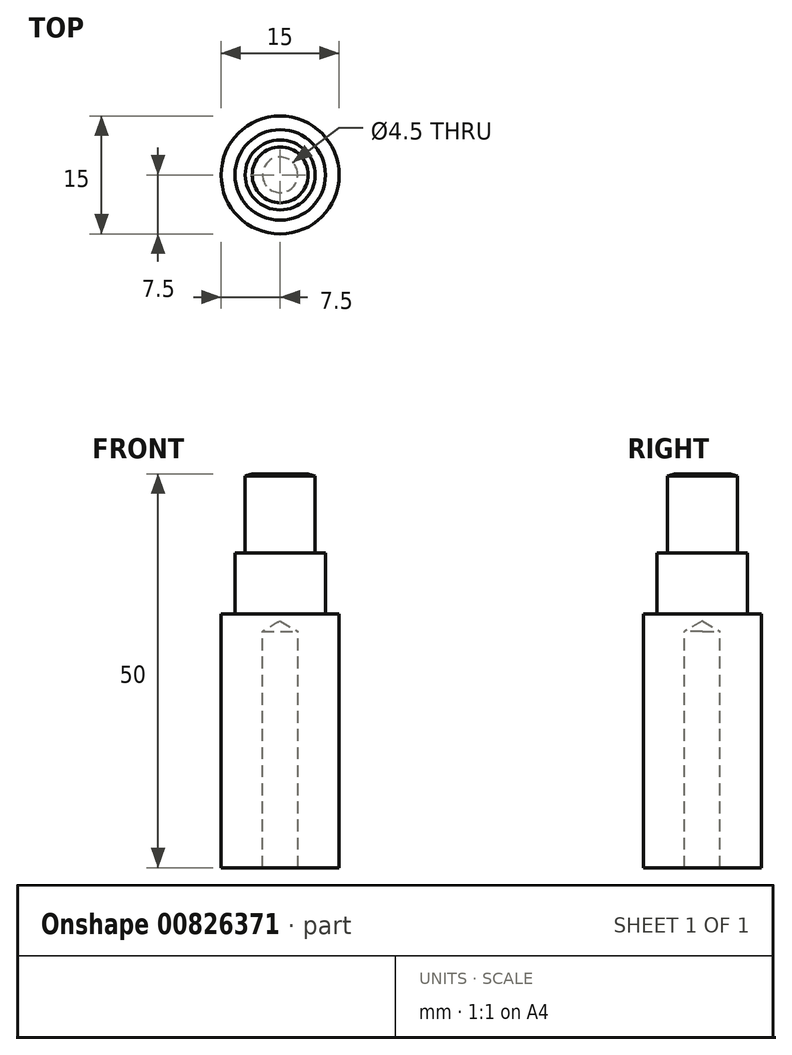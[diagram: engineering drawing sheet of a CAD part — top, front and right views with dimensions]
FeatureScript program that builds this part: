
annotation { "Feature Type Name" : "Feature", "Feature Type Description" : "" }
export const myFeature = defineFeature(function(context is Context, id is Id, definition is map)
    precondition{}
    {
        {
            var Q0;
            Q0=qCreatedBy(makeId("Front.planeOp"),FACE);
            var sketch = newSketch(context, id + "F0", { "sketchPlane" : qUnion([Q0])});
            skLineSegment(sketch, "E0", {"start": v(0, 0) * mm, "end": v(0, 50) * mm});
            skLineSegment(sketch, "E1", {"start": v(0, 50) * mm, "end": v(4.45, 50) * mm});
            skLineSegment(sketch, "E2", {"start": v(4.45, 50) * mm, "end": v(4.45, 40) * mm});
            skLineSegment(sketch, "E3", {"start": v(4.45, 40) * mm, "end": v(5.75, 40) * mm});
            skLineSegment(sketch, "E4", {"start": v(5.75, 40) * mm, "end": v(5.75, 32.2) * mm});
            skLineSegment(sketch, "E5", {"start": v(5.75, 32.2) * mm, "end": v(7.5, 32.2) * mm});
            skLineSegment(sketch, "E6", {"start": v(7.5, 32.2) * mm, "end": v(7.5, 0) * mm});
            skLineSegment(sketch, "E7", {"start": v(7.5, 0) * mm, "end": v(0, 0) * mm});
            skSolve(sketch);
        }
        {
            var Q0;
            Q0 = qSketchRegion(id + "F0", true);
            var Q1;
            Q1=sQuery(id+"F0.wireOp",EDGE,"E0");
            revolve(context, id + "F1", {"surfaceOperationType" : NewSurfaceOperationType.NEW, "entities" : qUnion([Q0]), "axis" : qUnion([Q1]), "revolveType" : RevolveType.FULL});
        }
        {
            var Q0;
            Q0=makeQuery(id+"F1.opRevolve","SWEPT_EDGE",EDGE,{"disambiguationData":[OSD([sQuery(id+"F0.wireOp",EDGE,"E1"),sQuery(id+"F0.wireOp",EDGE,"E2")])]});
            chamfer(context, id + "F2", {"entities" : qUnion([Q0]), "chamferType" : ChamferType.OFFSET_ANGLE, "width" : 8 * mm, "oppositeDirection" : false, "angle" : 15 * degree, "tangentPropagation" : true});
        }
        {
            var Q0;
            Q0=makeQuery(id+"F1.opRevolve","SWEPT_FACE",FACE,{"disambiguationData":[OSD([sQuery(id+"F0.wireOp",EDGE,"E7")])]});
            var sketch = newSketch(context, id + "F3", { "sketchPlane" : qUnion([Q0])});
            skPoint(sketch, "E8", {"position": v(0, 0) * mm});
            skSolve(sketch);
        }
        {
            var Q0;
            Q0=sQuery(id+"F3.wireOp",VERTEX,"E8");
            var Q1;
            Q1=makeQuery(id+"F1.opRevolve","SWEPT_BODY",BODY,{"disambiguationData":[OSD([sQuery(id+"F0.wireOp",EDGE,"E0"),sQuery(id+"F0.wireOp",EDGE,"E1"),sQuery(id+"F0.wireOp",EDGE,"E2"),sQuery(id+"F0.wireOp",EDGE,"E3"),sQuery(id+"F0.wireOp",EDGE,"E4"),sQuery(id+"F0.wireOp",EDGE,"E5"),sQuery(id+"F0.wireOp",EDGE,"E6"),sQuery(id+"F0.wireOp",EDGE,"E7")])]});
            hole(context, id + "F4", {"style" : HoleStyle.SIMPLE, "endStyle" : HoleEndStyle.BLIND, "standardTappedOrClearance" : lookupTablePath({ "fit" : "Normal", "standard" : "ISO", "size" : "M4", "type" : "Clearance" }), "standardBlindInLast" : lookupTablePath({ "fit" : "Normal", "standard" : "ISO", "size" : "M4", "type" : "Clearance" }), "holeDiameter" : 4.5 * mm, "majorDiameter" : 5 * mm, "holeDepth" : 30 * mm, "isTappedThrough" : true, "tappedDepth" : 12 * mm, "tapClearance" : 3, "locations" : qUnion([Q0]), "scope" : qUnion([Q1]), "startStyle" : HoleStartStyle.SKETCH});
        }
    });
